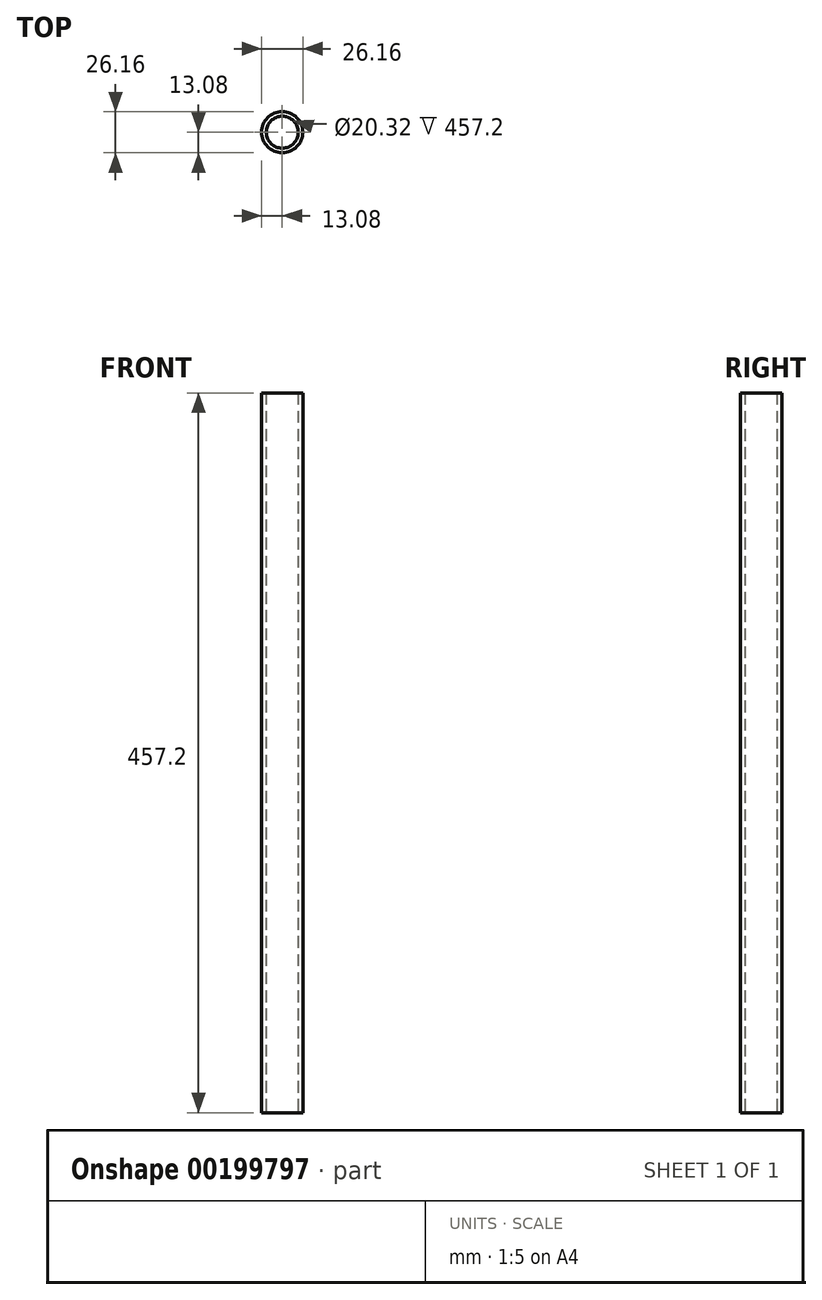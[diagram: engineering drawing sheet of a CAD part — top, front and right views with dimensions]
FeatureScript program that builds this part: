
annotation { "Feature Type Name" : "Feature", "Feature Type Description" : "" }
export const myFeature = defineFeature(function(context is Context, id is Id, definition is map)
    precondition{}
    {
        {
            var Q0;
            Q0=qCreatedBy(makeId("Top.planeOp"),FACE);
            var sketch = newSketch(context, id + "F0", { "sketchPlane" : qUnion([Q0])});
            skCircle(sketch, "E0", {"center": v(0, 0) * mm, "radius": 10.16 * mm});
            skCircle(sketch, "E1", {"center": v(0, 0) * mm, "radius": 13.08 * mm});
            skSolve(sketch);
        }
        {
            var Q0;
            Q0 = qSketchRegion(id + "F0", true);
            extrude(context, id + "F1", {"entities" : qUnion([Q0]), "depth" : 457.2 * mm});
        }
    });
